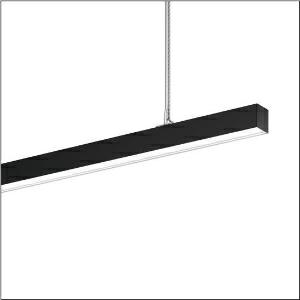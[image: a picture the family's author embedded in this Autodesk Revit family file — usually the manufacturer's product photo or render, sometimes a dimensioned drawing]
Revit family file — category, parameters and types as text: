
# Revit family: silica_r__21_51mx33da37bb_2abf
name_source: partatom
category: Lighting Fixtures
units: mm (PartAtom-declared; Revit-internal decimal feet)

## family parameters
Cut with Voids When Loaded = No
Host = Face
Light Source = No
Part Type = Normal
Room Calculation Point = No
Round Connector Dimension = Use Diameter
Shared = No

## types (1)
- --- (1 x LED, 5910 lm, 41.3 W, 3000K)
    Apparent Load = 41 VA
    CIE Flux Codes = 78 96 99 55 100
    Color Rendering = 80
    Color Temperature = 3000K
    Default Elevation = 1800 mm
    Description = Silica® 21, office luminaire, primary optical cover: prismatic diffuser, of PMMA, CAT 2 (L<= 3000cd/m²), light emission: direct/indirect distribution, primary light characteristic: symmetric, installation type: suspended mounting, LED, rated luminous flux: 5.910lm, luminous efficacy: 143lm/W, light colour: 830, colour temperature: 3000K, with terminal, 3+2-pole, max. 2.5mm², mains connection: 220..240V, AC, 50/60Hz, rated input power: 41.3W, luminaire housing, of aluminium, jet black (RAL 9005), length: 1.204mm, width: 53mm, height: 53mm, protection rating (complete): IP20, insulation class (complete): insulation class I (protective earthing), certification: CE, permissible operating ambient temperature: 0..+35°C, standard: EN 50419, packaging unit: 1 piece
    Height = 53 mm
    Lamp = 1 x LED
    Lamp Light Flux = 5910 lm
    Lamp Power = 41.3 W
    Lamp count = 1
    Length = 1204 mm
    Luminous efficacy = 143 lm/W
    Manufacturer = Siteco
    ModVariant = No
    Model = 51MX33DA37BB
    Mounting Place = Ceiling
    Mounting Type = Pendant
    Number of Poles = 1
    OnlyDefault = Yes
    Power Factor = 1
    Product Name = Silica® 21
    Product group = office luminaire | ceiling pendant
    ProductGroupID = 902
    Protection Class = Protection class I
    Protection Degree = IP 20
    RLX_Detail_Level = 1
    RLX_Emergency_Light_Flux = 0 lm
    RLX_Emergency_Type = 0
    RLX_Emergency_Type_DB = No
    RlxData = <blob elided: 26081 chars, md5=47b06cd8>
    Socket = socket
    Standby Power = 0 W
    System Light Flux = 5910 lm
    System Power = 41 W
    Type Comments = factory setting: luminous flux: 100 % | dim-lin: 254 | 345 mA
    Type Image = l_1335856.jpg
    URL = http://relux.com
    VarID = @adj_087879
    Voltage = 0 V
    Weight = 0.00 kg
    Width = 53 mm

## geometry (parser evidence)
native form markers: Blend x4, Sweep x14
no freeform markers — native parametric forms only
